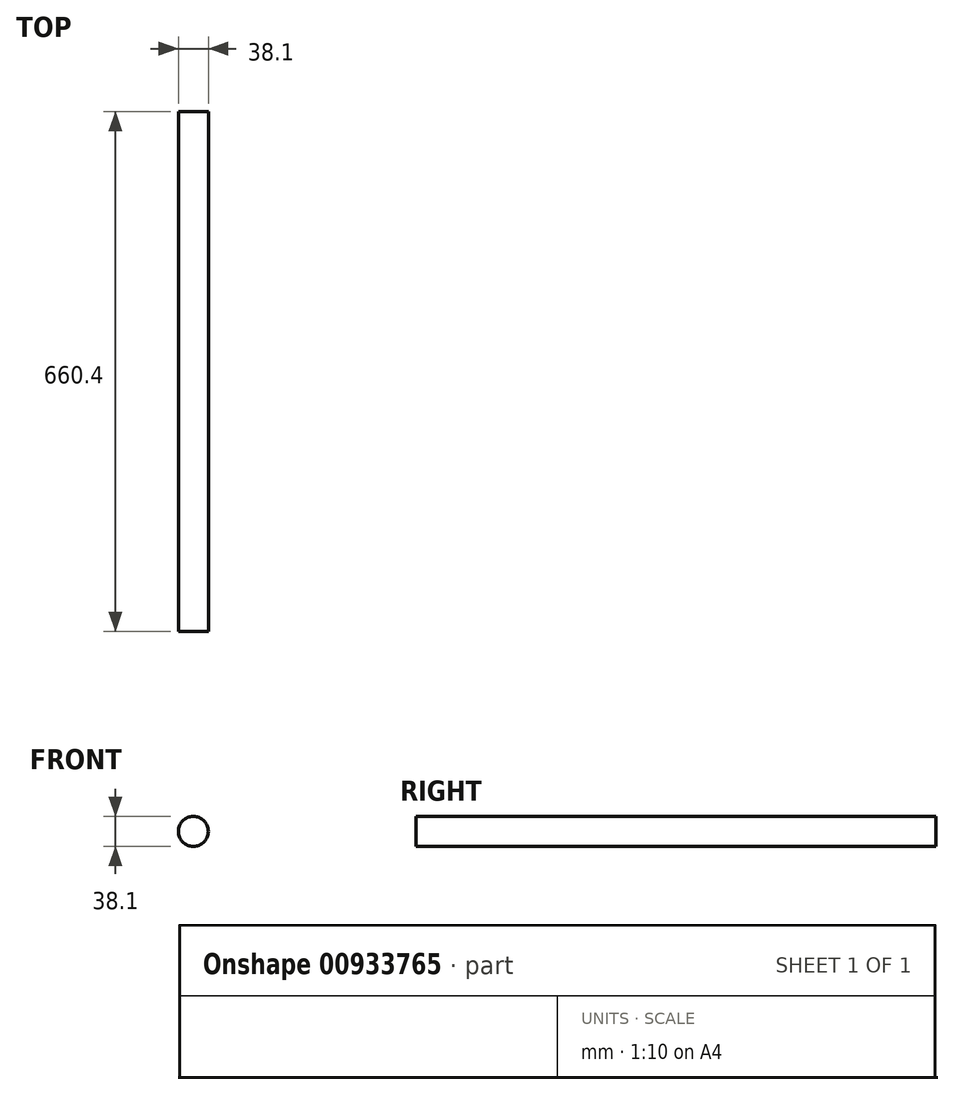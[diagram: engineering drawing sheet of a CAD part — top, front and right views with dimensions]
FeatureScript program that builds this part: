
annotation { "Feature Type Name" : "Feature", "Feature Type Description" : "" }
export const myFeature = defineFeature(function(context is Context, id is Id, definition is map)
    precondition{}
    {
        {
            var Q0;
            Q0=qCreatedBy(makeId("Front.planeOp"),FACE);
            var sketch = newSketch(context, id + "F0", { "sketchPlane" : qUnion([Q0])});
            skCircle(sketch, "E0", {"center": v(0, 0) * mm, "radius": 19.05 * mm});
            skSolve(sketch);
        }
        {
            var Q0;
            Q0=makeQuery(id+"F0.imprint","IMPRINT",FACE,{"disambiguationData":[TD([[makeQuery(id+"F0.imprint","IMPRINT",EDGE,{"derivedFrom":sQuery(id+"F0.wireOp",EDGE,"E0")}),1.0]])]});
            extrude(context, id + "F1", {"entities" : qUnion([Q0]), "depth" : 660.4 * mm, "offsetDistance" : 25.4 * mm});
        }
    });
